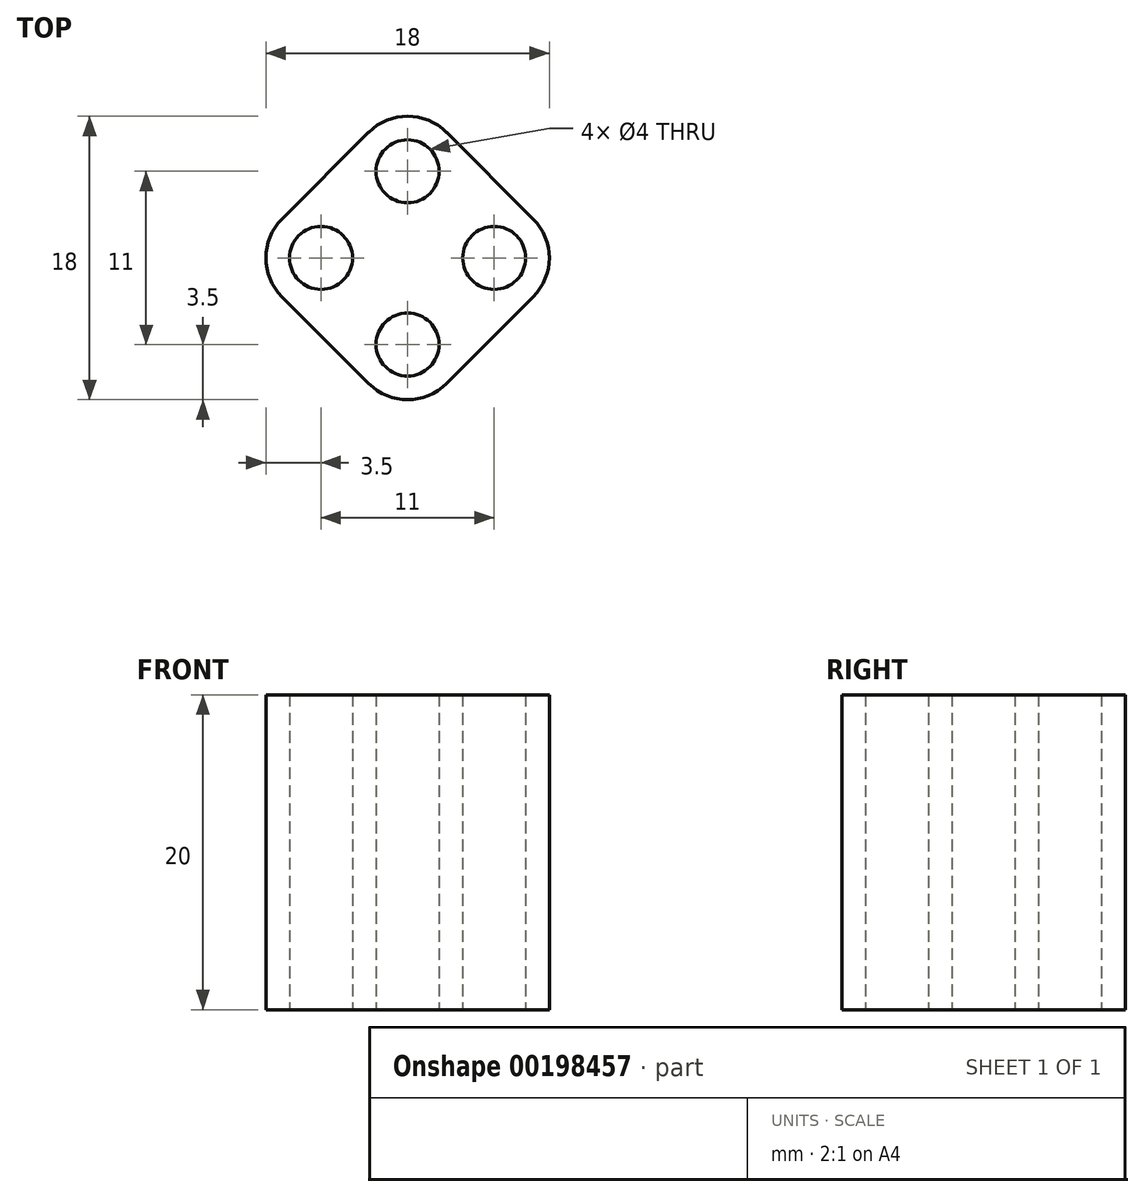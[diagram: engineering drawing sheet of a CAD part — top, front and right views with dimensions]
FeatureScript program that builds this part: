
annotation { "Feature Type Name" : "Feature", "Feature Type Description" : "" }
export const myFeature = defineFeature(function(context is Context, id is Id, definition is map)
    precondition{}
    {
        {
            var Q0;
            Q0=qCreatedBy(makeId("Top.planeOp"),FACE);
            var sketch = newSketch(context, id + "F0", { "sketchPlane" : qUnion([Q0])});
            skArc(sketch, "E0", {"start": v(-7.97, 2.47) * mm, "mid": v(-9, 0) * mm, "end": v(-7.97, -2.47) * mm});
            skCircle(sketch, "E1", {"center": v(-5.5, 0) * mm, "radius": 2 * mm});
            skArc(sketch, "E2.1.0", {"start": v(-2.47, -7.97) * mm, "mid": v(0, -9) * mm, "end": v(2.47, -7.97) * mm});
            skCircle(sketch, "E2.1.1", {"center": v(0, -5.5) * mm, "radius": 2 * mm});
            skArc(sketch, "E2.2.0", {"start": v(7.97, -2.47) * mm, "mid": v(9, 0) * mm, "end": v(7.97, 2.47) * mm});
            skCircle(sketch, "E2.2.1", {"center": v(5.5, 0) * mm, "radius": 2 * mm});
            skArc(sketch, "E2.3.0", {"start": v(2.47, 7.97) * mm, "mid": v(0, 9) * mm, "end": v(-2.47, 7.97) * mm});
            skCircle(sketch, "E2.3.1", {"center": v(0, 5.5) * mm, "radius": 2 * mm});
            skPoint(sketch, "E2.center", {"position": v(0, 0) * mm});
            skLineSegment(sketch, "E3", {"start": v(-7.97, 2.47) * mm, "end": v(-2.47, 7.97) * mm});
            skLineSegment(sketch, "E4", {"start": v(-7.97, -2.47) * mm, "end": v(-2.47, -7.97) * mm});
            skLineSegment(sketch, "E5", {"start": v(2.47, 7.97) * mm, "end": v(7.97, 2.47) * mm});
            skLineSegment(sketch, "E6", {"start": v(7.97, -2.47) * mm, "end": v(2.47, -7.97) * mm});
            skSolve(sketch);
        }
        {
            var Q0;
            Q0 = qSketchRegion(id + "F0", true);
            extrude(context, id + "F1", {"entities" : qUnion([Q0]), "depth" : 20 * mm});
        }
    });
